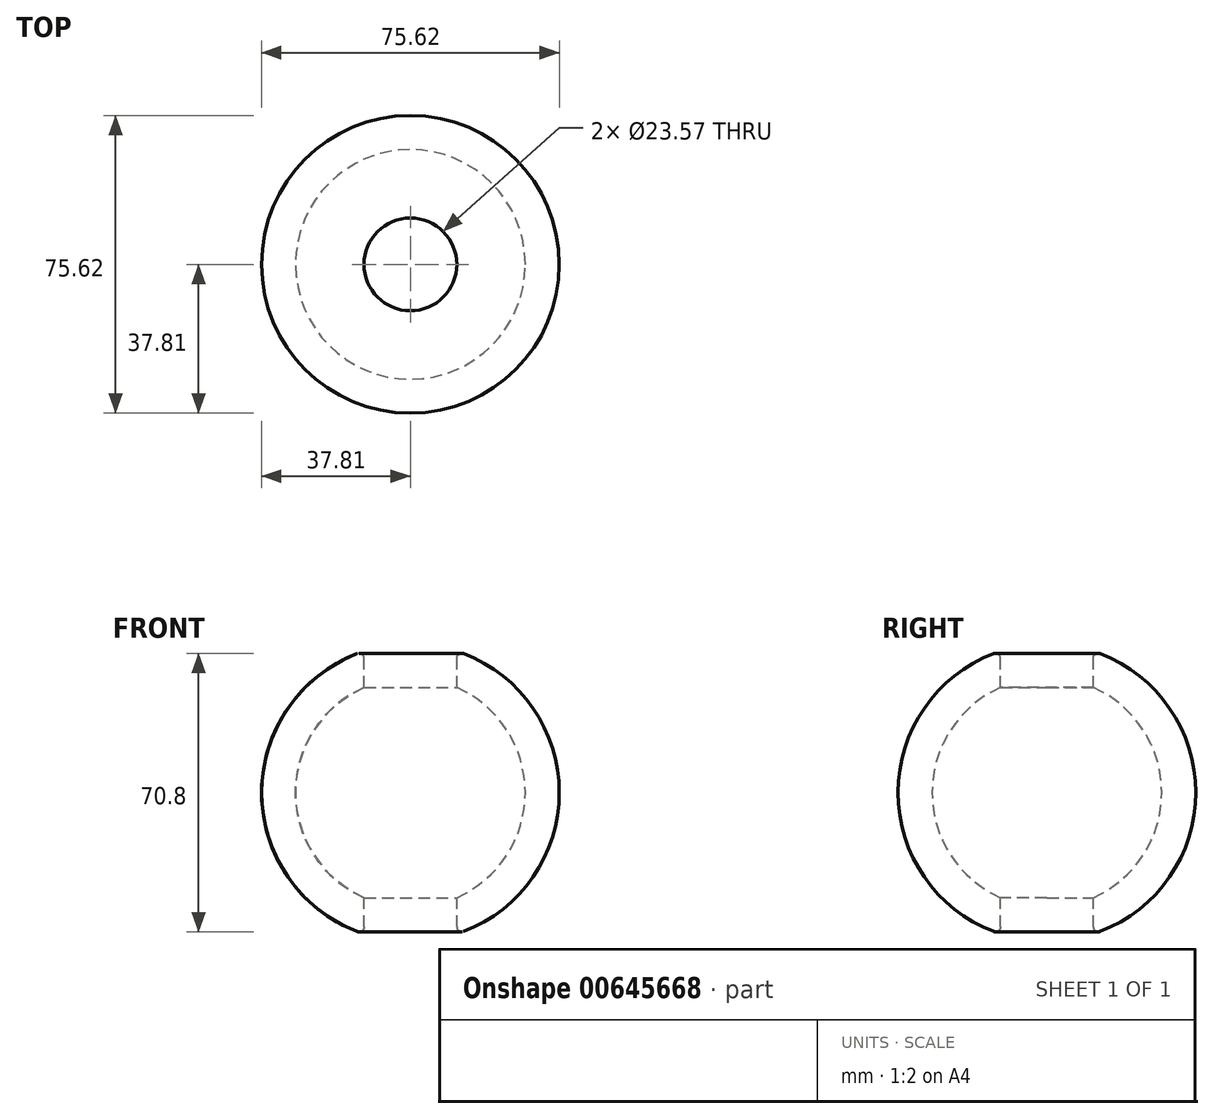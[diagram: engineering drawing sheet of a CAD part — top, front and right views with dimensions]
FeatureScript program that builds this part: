
annotation { "Feature Type Name" : "Feature", "Feature Type Description" : "" }
export const myFeature = defineFeature(function(context is Context, id is Id, definition is map)
    precondition{}
    {
        {
            var Q0;
            Q0=qCreatedBy(makeId("Front.planeOp"),FACE);
            var sketch = newSketch(context, id + "F0", { "sketchPlane" : qUnion([Q0])});
            skCircle(sketch, "E0", {"center": v(0, 0) * mm, "radius": 37.8 * mm});
            skCircle(sketch, "E1", {"center": v(0, 0) * mm, "radius": 29.18 * mm});
            skLineSegment(sketch, "E2", {"start": v(0, 50.1) * mm, "end": v(0, -50.5) * mm});
            skSolve(sketch);
        }
        {
            var Q0;
            {var subQ0=sQuery(id+"F0.wireOp",EDGE,"E2");var subQ1=sQuery(id+"F0.wireOp",EDGE,"E0");var subQ2=makeQuery(id+"F0.imprint","INTERSECT",VERTEX,{"disambiguationData":[OD(0.0)],"derivedFrom":[subQ1,subQ0]});Q0=makeQuery(id+"F0.imprint","IMPRINT",FACE,{"disambiguationData":[TD([[makeQuery(id+"F0.imprint","IMPRINT",EDGE,{"disambiguationData":[TD([[subQ2,-1.0]])],"derivedFrom":subQ1}),1.0]])]});}
            var Q1;
            Q1=sQuery(id+"F0.wireOp",EDGE,"E2");
            revolve(context, id + "F1", {"entities" : qUnion([Q0]), "axis" : qUnion([Q1]), "revolveType" : RevolveType.FULL});
        }
        {
            var Q0;
            Q0=qCreatedBy(makeId("Top.planeOp"),FACE);
            cPlane(context, id + "F2", {"entities" : qUnion([Q0]), "cplaneType" : CPlaneType.OFFSET, "offset" : 42.67 * mm, "width" : 152.4 * mm, "height" : 152.4 * mm});
        }
        {
            var Q0;
            Q0=qCreatedBy(id+"F2.planeOp",FACE);
            var sketch = newSketch(context, id + "F3", { "sketchPlane" : qUnion([Q0])});
            skCircle(sketch, "E3", {"center": v(0, 0) * mm, "radius": 11.78 * mm});
            skSolve(sketch);
        }
        {
            var Q0;
            Q0=makeQuery(id+"F3.imprint","IMPRINT",FACE,{"disambiguationData":[TD([[makeQuery(id+"F3.imprint","IMPRINT",EDGE,{"derivedFrom":sQuery(id+"F3.wireOp",EDGE,"E3")}),1.0]])]});
            extrude(context, id + "F4", {"entities" : qUnion([Q0]), "operationType" : NewBodyOperationType.REMOVE, "oppositeDirection" : true, "depth" : 127 * mm, "offsetDistance" : 25.4 * mm});
        }
        {
            var Q0;
            Q0=makeQuery(id+"F1.opRevolve","SWEPT_FACE",FACE,{"disambiguationData":[OSD([sQuery(id+"F0.wireOp",EDGE,"E0")])]});
            fillet(context, id + "F5", {"entities" : qUnion([Q0]), "radius" : 1.27 * mm, "tangentPropagation" : true, "allowEdgeOverflow" : false});
        }
    });
